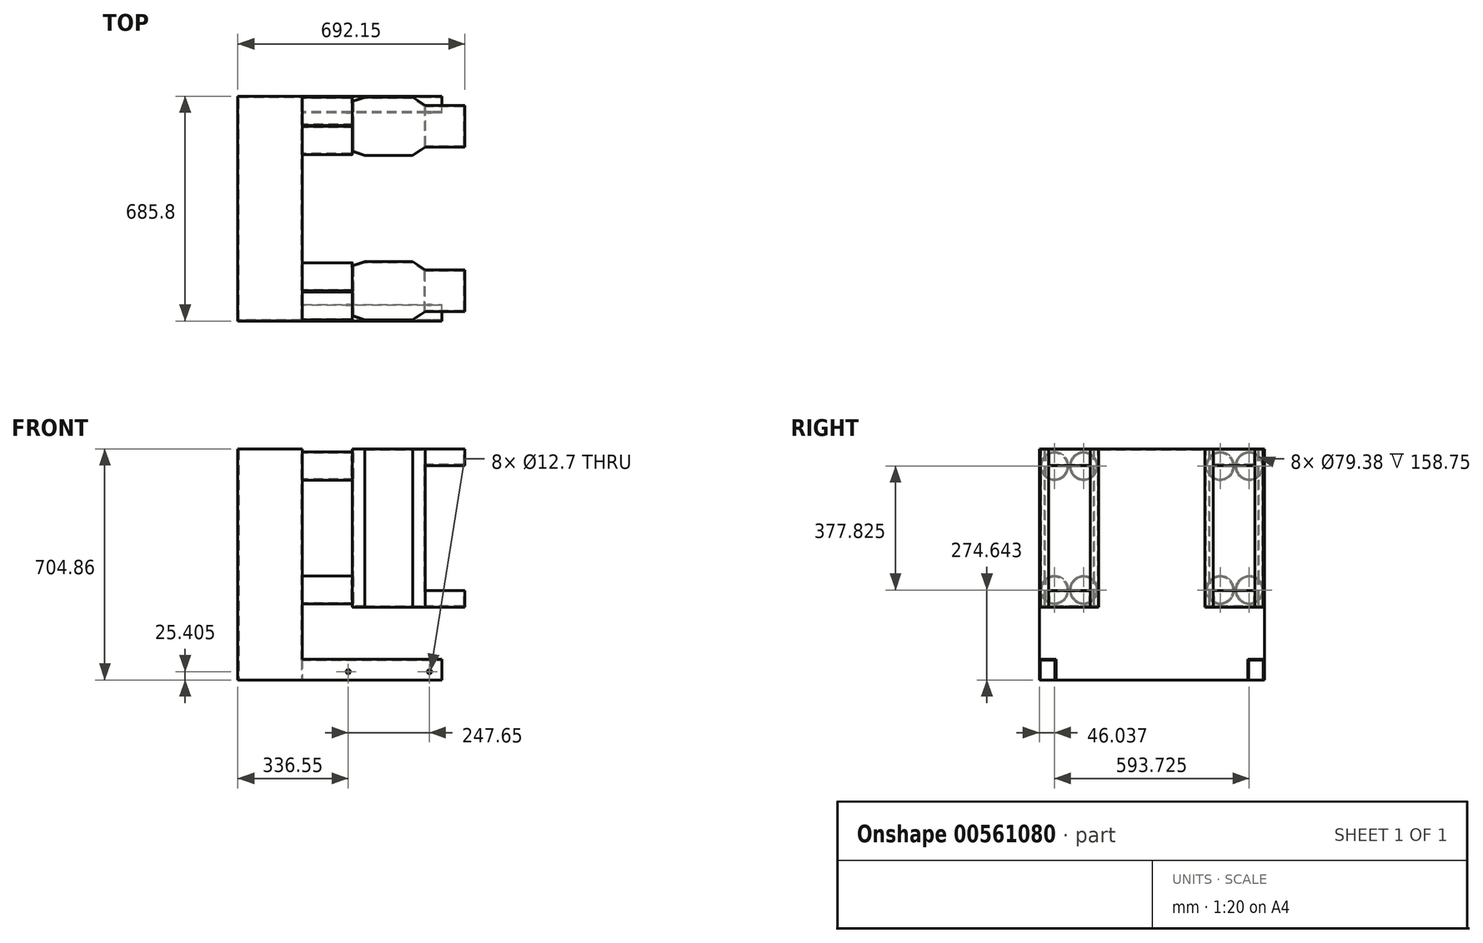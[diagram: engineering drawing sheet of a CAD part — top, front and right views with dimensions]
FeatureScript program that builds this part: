
annotation { "Feature Type Name" : "Feature", "Feature Type Description" : "" }
export const myFeature = defineFeature(function(context is Context, id is Id, definition is map)
    precondition{}
    {
        {
            var Q0;
            Q0=qCreatedBy(makeId("Front.planeOp"),FACE);
            var sketch = newSketch(context, id + "F0", { "sketchPlane" : qUnion([Q0])});
            skLineSegment(sketch, "E0", {"start": v(-114.3, 352.43) * mm, "end": v(-311.15, 352.43) * mm});
            skLineSegment(sketch, "E1", {"start": v(-311.15, 352.43) * mm, "end": v(-311.15, -352.43) * mm});
            skLineSegment(sketch, "E2", {"start": v(-311.15, -352.43) * mm, "end": v(311.15, -352.43) * mm});
            skLineSegment(sketch, "E3", {"start": v(311.15, -352.43) * mm, "end": v(311.15, -288.93) * mm});
            skLineSegment(sketch, "E4", {"start": v(311.15, -288.92) * mm, "end": v(-114.3, -288.93) * mm});
            skLineSegment(sketch, "E5", {"start": v(-114.3, -288.93) * mm, "end": v(-114.3, 352.43) * mm});
            skSolve(sketch);
        }
        {
            var Q0;
            Q0 = qSketchRegion(id + "F0", true);
            extrude(context, id + "F1", {"entities" : qUnion([Q0]), "depth" : 342.9 * mm, "offsetDistance" : 25.4 * mm, "hasSecondDirection" : true, "secondDirectionOppositeDirection" : true, "secondDirectionDepth" : 342.9 * mm});
        }
        {
            var Q0;
            Q0=makeQuery(id+"F1.opExtrude","SWEPT_FACE",FACE,{"disambiguationData":[OSD([sQuery(id+"F0.wireOp",EDGE,"E5")])]});
            var sketch = newSketch(context, id + "F2", { "sketchPlane" : qUnion([Q0])});
            skCircle(sketch, "E6", {"center": v(-296.86, 300.04) * mm, "radius": 42.86 * mm});
            skCircle(sketch, "E7", {"center": v(-207.96, 300.04) * mm, "radius": 42.86 * mm});
            skCircle(sketch, "E8", {"center": v(207.96, 300.04) * mm, "radius": 42.86 * mm});
            skCircle(sketch, "E9", {"center": v(296.86, 300.04) * mm, "radius": 42.86 * mm});
            skCircle(sketch, "E10", {"center": v(-296.86, -77.79) * mm, "radius": 42.86 * mm});
            skCircle(sketch, "E11", {"center": v(-207.96, -77.79) * mm, "radius": 42.86 * mm});
            skCircle(sketch, "E12", {"center": v(207.96, -77.79) * mm, "radius": 42.86 * mm});
            skCircle(sketch, "E13", {"center": v(296.86, -77.79) * mm, "radius": 42.86 * mm});
            skSolve(sketch);
        }
        {
            var Q0;
            Q0 = qSketchRegion(id + "F2", true);
            extrude(context, id + "F3", {"entities" : qUnion([Q0]), "operationType" : NewBodyOperationType.ADD, "depth" : 152.4 * mm, "offsetDistance" : 25.4 * mm});
        }
        {
            var Q0;
            Q0=makeQuery(id+"F1.opExtrude","SWEPT_FACE",FACE,{"disambiguationData":[OSD([sQuery(id+"F0.wireOp",EDGE,"E0")])]});
            var sketch = newSketch(context, id + "F4", { "sketchPlane" : qUnion([Q0])});
            skLineSegment(sketch, "E14", {"start": v(38.1, -174.63) * mm, "end": v(38.1, -327.03) * mm});
            skLineSegment(sketch, "E15", {"start": v(38.1, -327.03) * mm, "end": v(76.2, -339.73) * mm});
            skLineSegment(sketch, "E16", {"start": v(76.2, -339.73) * mm, "end": v(222.25, -339.73) * mm});
            skLineSegment(sketch, "E17", {"start": v(222.25, -339.73) * mm, "end": v(260.35, -314.33) * mm});
            skLineSegment(sketch, "E18", {"start": v(260.35, -314.33) * mm, "end": v(260.35, -187.33) * mm});
            skLineSegment(sketch, "E19", {"start": v(260.35, -187.33) * mm, "end": v(222.25, -161.93) * mm});
            skLineSegment(sketch, "E20", {"start": v(222.25, -161.93) * mm, "end": v(76.2, -161.93) * mm});
            skLineSegment(sketch, "E21", {"start": v(76.2, -161.93) * mm, "end": v(38.1, -174.63) * mm});
            skLineSegment(sketch, "E22", {"start": v(38.1, 327.03) * mm, "end": v(38.1, 174.63) * mm});
            skLineSegment(sketch, "E23", {"start": v(38.1, 174.63) * mm, "end": v(76.2, 161.93) * mm});
            skLineSegment(sketch, "E24", {"start": v(76.2, 161.93) * mm, "end": v(222.25, 161.93) * mm});
            skLineSegment(sketch, "E25", {"start": v(222.25, 161.93) * mm, "end": v(260.35, 187.33) * mm});
            skLineSegment(sketch, "E26", {"start": v(260.35, 187.33) * mm, "end": v(260.35, 314.33) * mm});
            skLineSegment(sketch, "E27", {"start": v(260.35, 314.33) * mm, "end": v(222.25, 339.73) * mm});
            skLineSegment(sketch, "E28", {"start": v(222.25, 339.73) * mm, "end": v(76.2, 339.73) * mm});
            skLineSegment(sketch, "E29", {"start": v(76.2, 339.73) * mm, "end": v(38.1, 327.03) * mm});
            skSolve(sketch);
        }
        {
            var Q0;
            Q0 = qSketchRegion(id + "F4", true);
            extrude(context, id + "F5", {"entities" : qUnion([Q0]), "operationType" : NewBodyOperationType.ADD, "oppositeDirection" : true, "depth" : 482.6 * mm, "offsetDistance" : 25.4 * mm});
        }
        {
            var Q0;
            Q0=makeQuery(id+"F5.opExtrude","SWEPT_FACE",FACE,{"disambiguationData":[OSD([sQuery(id+"F4.wireOp",EDGE,"E18")])]});
            var sketch = newSketch(context, id + "F6", { "sketchPlane" : qUnion([Q0])});
            skLineSegment(sketch, "E30.bottom", {"start": v(-314.33, 352.43) * mm, "end": v(-187.33, 352.43) * mm});
            skLineSegment(sketch, "E30.top", {"start": v(-314.33, 301.62) * mm, "end": v(-187.33, 301.62) * mm});
            skLineSegment(sketch, "E30.left", {"start": v(-314.33, 352.43) * mm, "end": v(-314.33, 301.62) * mm});
            skLineSegment(sketch, "E30.right", {"start": v(-187.33, 352.43) * mm, "end": v(-187.33, 301.62) * mm});
            skLineSegment(sketch, "E31.bottom", {"start": v(-314.33, -130.18) * mm, "end": v(-187.33, -130.18) * mm});
            skLineSegment(sketch, "E31.top", {"start": v(-314.33, -79.38) * mm, "end": v(-187.33, -79.38) * mm});
            skLineSegment(sketch, "E31.left", {"start": v(-314.33, -130.18) * mm, "end": v(-314.33, -79.38) * mm});
            skLineSegment(sketch, "E31.right", {"start": v(-187.33, -130.18) * mm, "end": v(-187.33, -79.38) * mm});
            skSolve(sketch);
        }
        {
            var Q0;
            Q0 = qSketchRegion(id + "F6", true);
            extrude(context, id + "F7", {"entities" : qUnion([Q0]), "operationType" : NewBodyOperationType.ADD, "depth" : 120.65 * mm, "offsetDistance" : 25.4 * mm});
        }
        {
            var Q0;
            Q0=makeQuery(id+"F5.opExtrude","SWEPT_FACE",FACE,{"disambiguationData":[OSD([sQuery(id+"F4.wireOp",EDGE,"E26")])]});
            var sketch = newSketch(context, id + "F8", { "sketchPlane" : qUnion([Q0])});
            skLineSegment(sketch, "E32.bottom", {"start": v(314.33, 352.43) * mm, "end": v(187.33, 352.43) * mm});
            skLineSegment(sketch, "E32.top", {"start": v(314.33, 301.62) * mm, "end": v(187.33, 301.62) * mm});
            skLineSegment(sketch, "E32.left", {"start": v(314.33, 352.43) * mm, "end": v(314.33, 301.62) * mm});
            skLineSegment(sketch, "E32.right", {"start": v(187.33, 352.43) * mm, "end": v(187.33, 301.62) * mm});
            skLineSegment(sketch, "E33.bottom", {"start": v(314.33, -130.18) * mm, "end": v(187.33, -130.18) * mm});
            skLineSegment(sketch, "E33.top", {"start": v(314.33, -79.37) * mm, "end": v(187.33, -79.38) * mm});
            skLineSegment(sketch, "E33.left", {"start": v(314.33, -130.18) * mm, "end": v(314.33, -79.37) * mm});
            skLineSegment(sketch, "E33.right", {"start": v(187.33, -130.18) * mm, "end": v(187.33, -79.38) * mm});
            skSolve(sketch);
        }
        {
            var Q0;
            Q0 = qSketchRegion(id + "F8", true);
            extrude(context, id + "F9", {"entities" : qUnion([Q0]), "operationType" : NewBodyOperationType.ADD, "depth" : 120.65 * mm, "offsetDistance" : 25.4 * mm});
        }
        {
            var Q0;
            Q0=makeQuery(id+"F1.opExtrude","SWEPT_FACE",FACE,{"disambiguationData":[OSD([sQuery(id+"F0.wireOp",EDGE,"E2")])]});
            var sketch = newSketch(context, id + "F10", { "sketchPlane" : qUnion([Q0])});
            skLineSegment(sketch, "E34.bottom", {"start": v(311.15, 292.1) * mm, "end": v(-114.3, 292.1) * mm});
            skLineSegment(sketch, "E34.top", {"start": v(311.15, -292.1) * mm, "end": v(-114.3, -292.1) * mm});
            skLineSegment(sketch, "E34.left", {"start": v(311.15, 292.1) * mm, "end": v(311.15, -292.1) * mm});
            skLineSegment(sketch, "E34.right", {"start": v(-114.3, 292.1) * mm, "end": v(-114.3, -292.1) * mm});
            skSolve(sketch);
        }
        {
            var Q0;
            Q0 = qSketchRegion(id + "F10", true);
            var Q1;
            Q1=makeQuery(id+"F1.opExtrude","SWEPT_FACE",FACE,{"disambiguationData":[OSD([sQuery(id+"F0.wireOp",EDGE,"E4")])]});
            extrude(context, id + "F11", {"entities" : qUnion([Q0]), "operationType" : NewBodyOperationType.REMOVE, "endBound" : BoundingType.UP_TO_SURFACE, "oppositeDirection" : true, "depth" : 25.4 * mm, "endBoundEntityFace" : qUnion([Q1]), "offsetDistance" : 25.4 * mm});
        }
        {
            var Q0;
            {var subQ1=sQuery(id+"F0.wireOp",EDGE,"E3");Q0=makeQuery(id+"F11.boolean.opBoolean","SPLIT",FACE,{"disambiguationData":[TD([makeQuery(id+"F11.opExtrude","SWEPT_FACE",FACE,{"disambiguationData":[OSD([sQuery(id+"F10.wireOp",EDGE,"E34.bottom")])]})])],"derivedFrom":makeQuery(id+"F1.opExtrude","SWEPT_FACE",FACE,{"disambiguationData":[OSD([subQ1])]})});}
            var Q1;
            Q1=makeQuery(id+"F1.opExtrude","SWEPT_FACE",FACE,{"disambiguationData":[OSD([sQuery(id+"F0.wireOp",EDGE,"E2")])]});
            var Q2;
            {var subQ1=sQuery(id+"F0.wireOp",EDGE,"E3");Q2=makeQuery(id+"F11.boolean.opBoolean","SPLIT",FACE,{"disambiguationData":[TD([makeQuery(id+"F11.opExtrude","SWEPT_FACE",FACE,{"disambiguationData":[OSD([sQuery(id+"F10.wireOp",EDGE,"E34.top")])]})])],"derivedFrom":makeQuery(id+"F1.opExtrude","SWEPT_FACE",FACE,{"disambiguationData":[OSD([subQ1])]})});}
            shell(context, id + "F12", {"entities" : qUnion([Q0, Q1, Q2]), "thickness" : 3.17 * mm});
        }
        {
            var Q0;
            Q0=makeQuery(id+"F1.opExtrude","CAP_FACE",FACE,{"disambiguationData":[OSD([sQuery(id+"F0.wireOp",EDGE,"E0"),sQuery(id+"F0.wireOp",EDGE,"E1"),sQuery(id+"F0.wireOp",EDGE,"E2"),sQuery(id+"F0.wireOp",EDGE,"E3"),sQuery(id+"F0.wireOp",EDGE,"E4"),sQuery(id+"F0.wireOp",EDGE,"E5")])],"isStart":false});
            var sketch = newSketch(context, id + "F13", { "sketchPlane" : qUnion([Q0])});
            skCircle(sketch, "E35", {"center": v(25.4, -327.03) * mm, "radius": 6.35 * mm});
            skCircle(sketch, "E36", {"center": v(273.05, -327.03) * mm, "radius": 6.35 * mm});
            skSolve(sketch);
        }
        {
            var Q0;
            Q0 = qSketchRegion(id + "F13", true);
            extrude(context, id + "F14", {"entities" : qUnion([Q0]), "operationType" : NewBodyOperationType.REMOVE, "endBound" : BoundingType.THROUGH_ALL, "oppositeDirection" : true, "depth" : 25.4 * mm, "offsetDistance" : 25.4 * mm});
        }
    });
